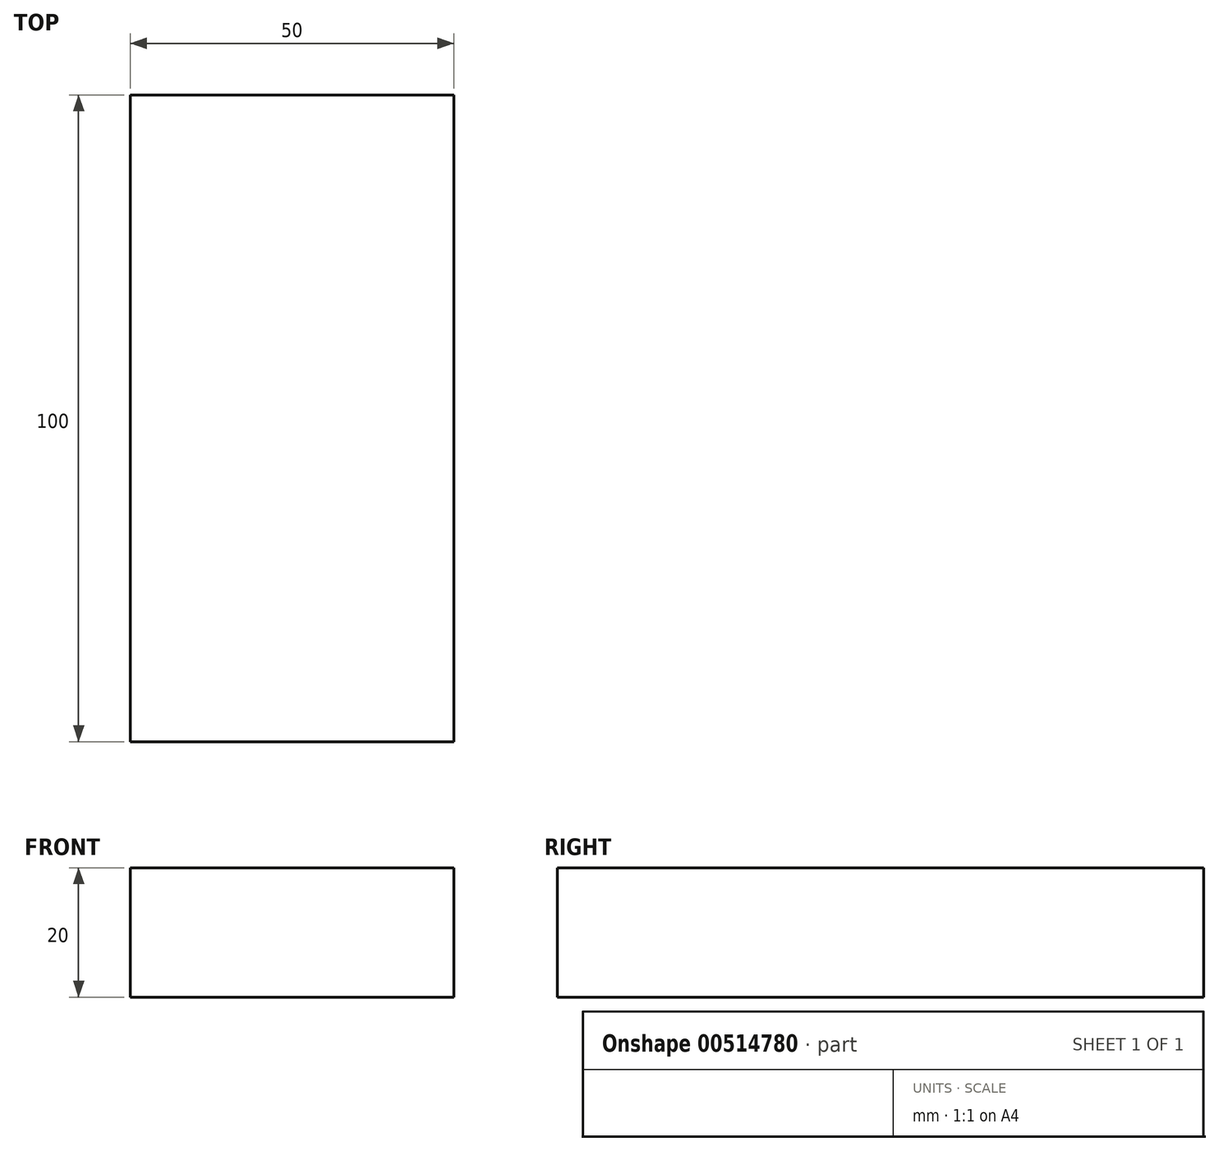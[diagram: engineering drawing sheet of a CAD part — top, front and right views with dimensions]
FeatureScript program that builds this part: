
annotation { "Feature Type Name" : "Feature", "Feature Type Description" : "" }
export const myFeature = defineFeature(function(context is Context, id is Id, definition is map)
    precondition{}
    {
        {
            var Q0;
            Q0=qCreatedBy(makeId("Front.planeOp"),FACE);
            var sketch = newSketch(context, id + "F0", { "sketchPlane" : qUnion([Q0])});
            skLineSegment(sketch, "E0.bottom", {"start": v(-25, -10) * mm, "end": v(25, -10) * mm});
            skLineSegment(sketch, "E0.top", {"start": v(-25, 10) * mm, "end": v(25, 10) * mm});
            skLineSegment(sketch, "E0.left", {"start": v(-25, -10) * mm, "end": v(-25, 10) * mm});
            skLineSegment(sketch, "E0.right", {"start": v(25, -10) * mm, "end": v(25, 10) * mm});
            skSolve(sketch);
        }
        {
            var Q0;
            Q0 = qSketchRegion(id + "F0", true);
            extrude(context, id + "F1", {"entities" : qUnion([Q0]), "depth" : 100 * mm, "offsetDistance" : 25.4 * mm});
        }
    });
